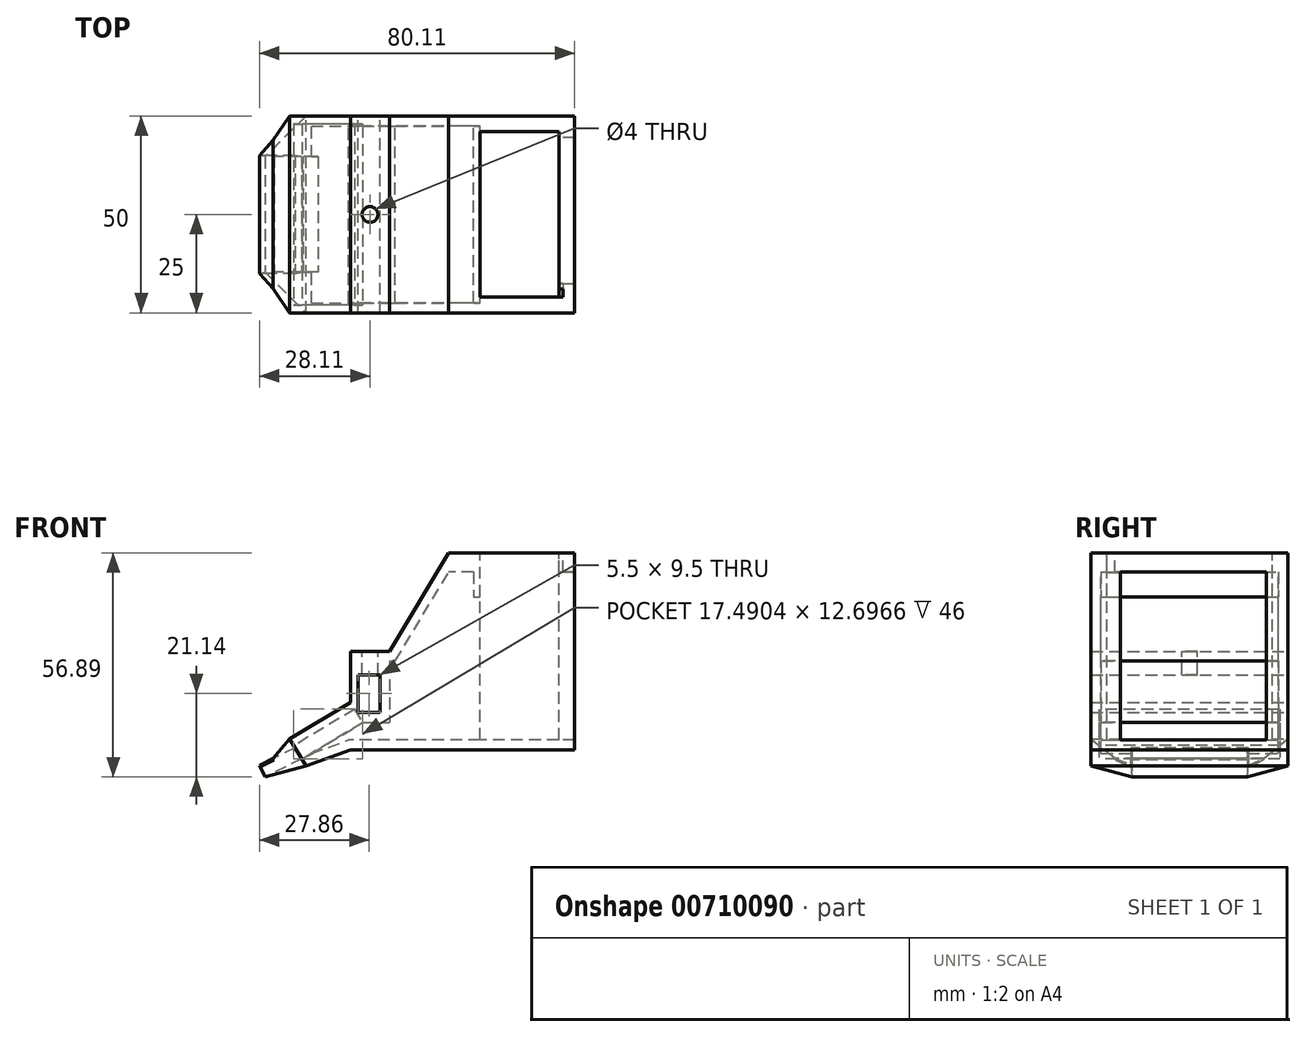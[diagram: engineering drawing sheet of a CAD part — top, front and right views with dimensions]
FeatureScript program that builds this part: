
annotation { "Feature Type Name" : "Feature", "Feature Type Description" : "" }
export const myFeature = defineFeature(function(context is Context, id is Id, definition is map)
    precondition{}
    {
        {
            var Q0;
            Q0=qCreatedBy(makeId("Front.planeOp"),FACE);
            var sketch = newSketch(context, id + "F0", { "sketchPlane" : qUnion([Q0])});
            skLineSegment(sketch, "E0", {"start": v(0, 0) * mm, "end": v(0, 25) * mm});
            skLineSegment(sketch, "E1", {"start": v(0, 25) * mm, "end": v(20, 25) * mm});
            skLineSegment(sketch, "E2", {"start": v(20, 25) * mm, "end": v(20, 0) * mm});
            skLineSegment(sketch, "E3", {"start": v(20, 0) * mm, "end": v(0, 0) * mm});
            skLineSegment(sketch, "E4.bottom", {"start": v(2, 19) * mm, "end": v(7.5, 19) * mm});
            skLineSegment(sketch, "E4.top", {"start": v(2, 9.5) * mm, "end": v(7.5, 9.5) * mm});
            skLineSegment(sketch, "E4.left", {"start": v(2, 19) * mm, "end": v(2, 9.5) * mm});
            skLineSegment(sketch, "E4.right", {"start": v(7.5, 19) * mm, "end": v(7.5, 9.5) * mm});
            skLineSegment(sketch, "E5", {"start": v(10, 25) * mm, "end": v(25, 50) * mm});
            skLineSegment(sketch, "E6", {"start": v(25, 50) * mm, "end": v(25, 0) * mm});
            skLineSegment(sketch, "E7", {"start": v(25, 0) * mm, "end": v(20, 0) * mm});
            skLineSegment(sketch, "E8", {"start": v(0, 12) * mm, "end": v(-15.4, 2.75) * mm});
            skLineSegment(sketch, "E9", {"start": v(-15.4, 2.75) * mm, "end": v(-11.28, -4.1) * mm});
            skLineSegment(sketch, "E10", {"start": v(-11.28, -4.1) * mm, "end": v(0, 0) * mm});
            skSolve(sketch);
        }
        {
            var Q0;
            Q0=makeQuery(id+"F0.imprint","IMPRINT",FACE,{"disambiguationData":[TD([[makeQuery(id+"F0.imprint","IMPRINT",EDGE,{"derivedFrom":sQuery(id+"F0.wireOp",EDGE,"E0")}),-1.0]])]});
            var Q1;
            {var subQ1=sQuery(id+"F0.wireOp",EDGE,"E2");Q1=makeQuery(id+"F0.imprint","IMPRINT",FACE,{"disambiguationData":[TD([[makeQuery(id+"F0.imprint","IMPRINT",EDGE,{"derivedFrom":subQ1}),1.0]])]});}
            var Q2;
            {var subQ2=sQuery(id+"F0.wireOp",EDGE,"E8");Q2=makeQuery(id+"F0.imprint","IMPRINT",FACE,{"disambiguationData":[TD([[makeQuery(id+"F0.imprint","IMPRINT",EDGE,{"derivedFrom":subQ2}),1.0]])]});}
            extrude(context, id + "F1", {"entities" : qUnion([Q0, Q1, Q2]), "depth" : 50 * mm, "offsetDistance" : 25 * mm});
        }
        {
            var Q0;
            Q0=makeQuery(id+"F1.opExtrude","SWEPT_FACE",FACE,{"disambiguationData":[OSD([sQuery(id+"F0.wireOp",EDGE,"E6")])]});
            shell(context, id + "F2", {"entities" : qUnion([Q0]), "thickness" : 2.5 * mm});
        }
        {
            var Q0;
            Q0=makeQuery(id+"F1.opExtrude","SWEPT_FACE",FACE,{"disambiguationData":[OSD([sQuery(id+"F0.wireOp",EDGE,"E9")])]});
            var sketch = newSketch(context, id + "F3", { "sketchPlane" : qUnion([Q0])});
            skLineSegment(sketch, "E11.bottom", {"start": v(2, 8.29) * mm, "end": v(48, 8.29) * mm});
            skLineSegment(sketch, "E11.top", {"start": v(2, 4.29) * mm, "end": v(48, 4.29) * mm});
            skLineSegment(sketch, "E11.left", {"start": v(2, 8.29) * mm, "end": v(2, 4.29) * mm});
            skLineSegment(sketch, "E11.right", {"start": v(48, 8.29) * mm, "end": v(48, 4.29) * mm});
            skSolve(sketch);
        }
        {
            var Q0;
            Q0=makeQuery(id+"F3.imprint","IMPRINT",FACE,{"disambiguationData":[TD([[makeQuery(id+"F3.imprint","IMPRINT",EDGE,{"derivedFrom":sQuery(id+"F3.wireOp",EDGE,"E11.bottom")}),-1.0]])]});
            extrude(context, id + "F4", {"entities" : qUnion([Q0]), "operationType" : NewBodyOperationType.REMOVE, "oppositeDirection" : true, "depth" : 18 * mm, "offsetDistance" : 25 * mm});
        }
        {
            var Q0;
            Q0=makeQuery(id+"F1.opExtrude","SWEPT_FACE",FACE,{"disambiguationData":[OSD([sQuery(id+"F0.wireOp",EDGE,"E6")])]});
            extrude(context, id + "F5", {"entities" : qUnion([Q0]), "operationType" : NewBodyOperationType.ADD, "depth" : 30 * mm, "offsetDistance" : 25 * mm});
        }
        {
            var Q0;
            {var subQ0=sQuery(id+"F0.wireOp",EDGE,"E6");var subQ1=sQuery(id+"F0.wireOp",EDGE,"E5");Q0=makeQuery(id+"F5.opExtrude","SWEPT_FACE",FACE,{"disambiguationData":[OSD([subQ1,subQ0]),TDD([makeQuery(id+"F2.opShell","OFFSET_EDGE",EDGE,{"disambiguationData":[OSD([subQ1,subQ0])]})])]});}
            var sketch = newSketch(context, id + "F6", { "sketchPlane" : qUnion([Q0])});
            skLineSegment(sketch, "E12", {"start": v(53, 47.5) * mm, "end": v(53, 2.5) * mm});
            skLineSegment(sketch, "E13", {"start": v(53, 44.5) * mm, "end": v(55, 44.5) * mm});
            skLineSegment(sketch, "E14", {"start": v(55, 44.5) * mm, "end": v(55, 5.5) * mm});
            skLineSegment(sketch, "E15", {"start": v(55, 5.5) * mm, "end": v(53, 5.5) * mm});
            skSolve(sketch);
        }
        {
            var Q0;
            {var subQ5=sQuery(id+"F6.wireOp",EDGE,"E13");Q0=makeQuery(id+"F6.imprint","IMPRINT",FACE,{"disambiguationData":[TD([[makeQuery(id+"F6.imprint","IMPRINT",EDGE,{"derivedFrom":subQ5}),1.0]])]});}
            var Q1;
            {var subQ5=sQuery(id+"F6.wireOp",EDGE,"E15");Q1=makeQuery(id+"F6.imprint","IMPRINT",FACE,{"disambiguationData":[TD([[makeQuery(id+"F6.imprint","IMPRINT",EDGE,{"derivedFrom":subQ5}),1.0]])]});}
            extrude(context, id + "F7", {"entities" : qUnion([Q0, Q1]), "operationType" : NewBodyOperationType.ADD, "endBound" : BoundingType.UP_TO_NEXT, "depth" : 25 * mm, "offsetDistance" : 25 * mm});
        }
        {
            var Q0;
            {var subQ0=sQuery(id+"F0.wireOp",EDGE,"E6");var subQ1=sQuery(id+"F0.wireOp",EDGE,"E5");Q0=makeQuery(id+"F5.opExtrude","SWEPT_FACE",FACE,{"disambiguationData":[OSD([subQ1,subQ0]),TDD([makeQuery(id+"F1.opExtrude","SWEPT_EDGE",EDGE,{"disambiguationData":[OSD([subQ1,subQ0])]})])]});}
            var sketch = newSketch(context, id + "F8", { "sketchPlane" : qUnion([Q0])});
            skLineSegment(sketch, "E16.bottom", {"start": v(33, -46) * mm, "end": v(53, -46) * mm});
            skLineSegment(sketch, "E16.top", {"start": v(33, -4) * mm, "end": v(53, -4) * mm});
            skLineSegment(sketch, "E16.left", {"start": v(33, -46) * mm, "end": v(33, -4) * mm});
            skLineSegment(sketch, "E16.right", {"start": v(53, -46) * mm, "end": v(53, -4) * mm});
            skSolve(sketch);
        }
        {
            var Q0;
            Q0=makeQuery(id+"F8.imprint","IMPRINT",FACE,{"disambiguationData":[TD([[makeQuery(id+"F8.imprint","IMPRINT",EDGE,{"derivedFrom":sQuery(id+"F8.wireOp",EDGE,"E16.bottom")}),1.0]])]});
            extrude(context, id + "F9", {"entities" : qUnion([Q0]), "operationType" : NewBodyOperationType.REMOVE, "endBound" : BoundingType.UP_TO_NEXT, "oppositeDirection" : true, "depth" : 25 * mm, "offsetDistance" : 25 * mm});
        }
        {
            var Q0;
            {var subQ0=sQuery(id+"F0.wireOp",EDGE,"E6");var subQ1=sQuery(id+"F0.wireOp",EDGE,"E10");var subQ2=sQuery(id+"F0.wireOp",EDGE,"E9");var subQ3=sQuery(id+"F0.wireOp",EDGE,"E8");var subQ4=sQuery(id+"F0.wireOp",EDGE,"E7");var subQ5=sQuery(id+"F0.wireOp",EDGE,"E5");var subQ6=sQuery(id+"F0.wireOp",EDGE,"E4.right");var subQ7=sQuery(id+"F0.wireOp",EDGE,"E4.left");var subQ8=sQuery(id+"F0.wireOp",EDGE,"E4.top");var subQ9=sQuery(id+"F0.wireOp",EDGE,"E4.bottom");var subQ10=sQuery(id+"F0.wireOp",EDGE,"E3");var subQ11=sQuery(id+"F0.wireOp",EDGE,"E1");var subQ12=sQuery(id+"F0.wireOp",EDGE,"E0");Q0=makeQuery(id+"F5.boolean.opBoolean","MERGE",FACE,{"derivedFrom":[makeQuery(id+"F2.opShell","OFFSET_FACE",FACE,{"disambiguationData":[OSD([subQ12,subQ11,subQ10,subQ9,subQ8,subQ7,subQ6,subQ5,subQ0,subQ4,subQ3,subQ2,subQ1]),TDD([makeQuery(id+"F1.opExtrude","CAP_FACE",FACE,{"disambiguationData":[OSD([subQ12,subQ11,subQ10,subQ9,subQ8,subQ7,subQ6,subQ5,subQ0,subQ4,subQ3,subQ2,subQ1])],"isStart":true})])]}),makeQuery(id+"F5.opExtrude","SWEPT_FACE",FACE,{"disambiguationData":[OSD([subQ0]),TDD([makeQuery(id+"F2.opShell","OFFSET_EDGE",EDGE,{"disambiguationData":[OSD([subQ0]),TDD([makeQuery(id+"F1.opExtrude","CAP_EDGE",EDGE,{"disambiguationData":[OSD([subQ0])],"isStart":true})])]})])]})]});}
            var sketch = newSketch(context, id + "F10", { "sketchPlane" : qUnion([Q0])});
            skLineSegment(sketch, "E17.bottom", {"start": v(31.3, 45.14) * mm, "end": v(33, 45.14) * mm});
            skLineSegment(sketch, "E17.top", {"start": v(31.3, 41.86) * mm, "end": v(33, 41.86) * mm});
            skLineSegment(sketch, "E17.left", {"start": v(31.3, 45.14) * mm, "end": v(31.3, 41.86) * mm});
            skLineSegment(sketch, "E17.right", {"start": v(33, 45.14) * mm, "end": v(33, 41.86) * mm});
            skSolve(sketch);
        }
        {
            var Q0;
            Q0=makeQuery(id+"F10.imprint","IMPRINT",FACE,{"disambiguationData":[TD([[makeQuery(id+"F10.imprint","IMPRINT",EDGE,{"derivedFrom":sQuery(id+"F10.wireOp",EDGE,"E17.bottom")}),1.0]])]});
            extrude(context, id + "F11", {"entities" : qUnion([Q0]), "operationType" : NewBodyOperationType.ADD, "endBound" : BoundingType.UP_TO_NEXT, "depth" : 25 * mm, "offsetDistance" : 25 * mm});
        }
        {
            var Q0;
            {var subQ0=sQuery(id+"F0.wireOp",EDGE,"E6");var subQ1=sQuery(id+"F0.wireOp",EDGE,"E5");Q0=makeQuery(id+"F5.opExtrude","SWEPT_FACE",FACE,{"disambiguationData":[OSD([subQ1,subQ0]),TDD([makeQuery(id+"F1.opExtrude","SWEPT_EDGE",EDGE,{"disambiguationData":[OSD([subQ1,subQ0])]})])]});}
            var sketch = newSketch(context, id + "F12", { "sketchPlane" : qUnion([Q0])});
            skLineSegment(sketch, "E18.bottom", {"start": v(53, -46) * mm, "end": v(54, -46) * mm});
            skLineSegment(sketch, "E18.top", {"start": v(53, -44) * mm, "end": v(54, -44) * mm});
            skLineSegment(sketch, "E18.left", {"start": v(53, -46) * mm, "end": v(53, -44) * mm});
            skLineSegment(sketch, "E18.right", {"start": v(54, -46) * mm, "end": v(54, -44) * mm});
            skSolve(sketch);
        }
        {
            var Q0;
            Q0=makeQuery(id+"F12.imprint","IMPRINT",FACE,{"disambiguationData":[TD([[makeQuery(id+"F12.imprint","IMPRINT",EDGE,{"derivedFrom":sQuery(id+"F12.wireOp",EDGE,"E18.bottom")}),1.0]])]});
            extrude(context, id + "F13", {"entities" : qUnion([Q0]), "operationType" : NewBodyOperationType.REMOVE, "oppositeDirection" : true, "depth" : 5 * mm, "offsetDistance" : 25 * mm});
        }
        {
            var Q0;
            {var subQ1=sQuery(id+"F0.wireOp",EDGE,"E6");var subQ2=sQuery(id+"F0.wireOp",EDGE,"E5");var subQ19=makeQuery(id+"F9.opExtrude","SWEPT_FACE",FACE,{"disambiguationData":[OSD([sQuery(id+"F8.wireOp",EDGE,"E16.bottom")])]});Q0=makeQuery(id+"F11.boolean.opBoolean","SPLIT",FACE,{"disambiguationData":[TD([makeQuery(id+"F9.boolean.opBoolean","COPY",FACE,{"derivedFrom":subQ19})])],"derivedFrom":makeQuery(id+"F9.boolean.opBoolean","SPLIT",FACE,{"disambiguationData":[TD([makeQuery(id+"F2.opShell","OFFSET_FACE",FACE,{"disambiguationData":[OSD([subQ2])]})])],"derivedFrom":makeQuery(id+"F5.opExtrude","SWEPT_FACE",FACE,{"disambiguationData":[OSD([subQ2,subQ1]),TDD([makeQuery(id+"F2.opShell","OFFSET_EDGE",EDGE,{"disambiguationData":[OSD([subQ2,subQ1])]})])]})})});}
            var Q1;
            {var subQ1=sQuery(id+"F0.wireOp",EDGE,"E6");var subQ2=sQuery(id+"F0.wireOp",EDGE,"E5");var subQ4=makeQuery(id+"F9.opExtrude","SWEPT_FACE",FACE,{"disambiguationData":[OSD([sQuery(id+"F8.wireOp",EDGE,"E16.top")])]});Q1=makeQuery(id+"F11.boolean.opBoolean","SPLIT",FACE,{"disambiguationData":[TD([makeQuery(id+"F9.boolean.opBoolean","COPY",FACE,{"derivedFrom":subQ4})])],"derivedFrom":makeQuery(id+"F9.boolean.opBoolean","SPLIT",FACE,{"disambiguationData":[TD([makeQuery(id+"F2.opShell","OFFSET_FACE",FACE,{"disambiguationData":[OSD([subQ2])]})])],"derivedFrom":makeQuery(id+"F5.opExtrude","SWEPT_FACE",FACE,{"disambiguationData":[OSD([subQ2,subQ1]),TDD([makeQuery(id+"F2.opShell","OFFSET_EDGE",EDGE,{"disambiguationData":[OSD([subQ2,subQ1])]})])]})})});}
            extrude(context, id + "F14", {"entities" : qUnion([Q0, Q1]), "operationType" : NewBodyOperationType.ADD, "endBound" : BoundingType.UP_TO_NEXT, "depth" : 25 * mm, "offsetDistance" : 25 * mm});
        }
        {
            var Q0;
            {var subQ0=sQuery(id+"F0.wireOp",EDGE,"E6");var subQ1=sQuery(id+"F0.wireOp",EDGE,"E5");var subQ2=makeQuery(id+"F5.opExtrude","CAP_EDGE",EDGE,{"disambiguationData":[OSD([subQ1,subQ0]),TDD([makeQuery(id+"F2.opShell","OFFSET_EDGE",EDGE,{"disambiguationData":[OSD([subQ1,subQ0])]})])],"isStart":false});var subQ3=sQuery(id+"F6.wireOp",EDGE,"E14");Q0=makeQuery(id+"F7.boolean.opBoolean","MERGE",FACE,{"derivedFrom":[makeQuery(id+"F5.opExtrude","CAP_FACE",FACE,{"disambiguationData":[OSD([subQ0])],"isStart":false}),makeQuery(id+"F7.opExtrude","SWEPT_FACE",FACE,{"disambiguationData":[OSD([subQ1,subQ0]),TDD([makeQuery(id+"F6.imprint","IMPRINT",EDGE,{"disambiguationData":[TD([[makeQuery(id+"F6.imprint","INTERSECT",VERTEX,{"derivedFrom":[subQ2,subQ3,sQuery(id+"F6.wireOp",EDGE,"E15")]}),-1.0]])],"derivedFrom":subQ2})])]}),makeQuery(id+"F7.opExtrude","SWEPT_FACE",FACE,{"disambiguationData":[OSD([subQ1,subQ0]),TDD([makeQuery(id+"F6.imprint","IMPRINT",EDGE,{"disambiguationData":[TD([[makeQuery(id+"F6.imprint","INTERSECT",VERTEX,{"derivedFrom":[subQ2,sQuery(id+"F6.wireOp",EDGE,"E13"),subQ3]}),1.0]])],"derivedFrom":subQ2})])]})]});}
            extrude(context, id + "F15", {"entities" : qUnion([Q0]), "operationType" : NewBodyOperationType.ADD, "depth" : 5 * mm, "offsetDistance" : 25 * mm});
        }
        {
            var Q0;
            Q0=makeQuery(id+"F11.opExtrude","SWEPT_FACE",FACE,{"disambiguationData":[OSD([sQuery(id+"F10.wireOp",EDGE,"E17.top")])]});
            extrude(context, id + "F16", {"entities" : qUnion([Q0]), "operationType" : NewBodyOperationType.ADD, "depth" : 3 * mm, "offsetDistance" : 25 * mm});
        }
        {
            var Q0;
            {var subQ0=sQuery(id+"F6.wireOp",EDGE,"E13");Q0=makeQuery(id+"F15.boolean.opBoolean","MERGE",FACE,{"derivedFrom":[makeQuery(id+"F7.opExtrude","SWEPT_FACE",FACE,{"disambiguationData":[OSD([subQ0])]}),makeQuery(id+"F15.opExtrude","SWEPT_FACE",FACE,{"disambiguationData":[OSD([sQuery(id+"F0.wireOp",EDGE,"E5"),sQuery(id+"F0.wireOp",EDGE,"E6"),subQ0,sQuery(id+"F6.wireOp",EDGE,"E14")])]})]});}
            extrude(context, id + "F17", {"entities" : qUnion([Q0]), "operationType" : NewBodyOperationType.ADD, "depth" : 2 * mm, "offsetDistance" : 25 * mm});
        }
        {
            var Q0;
            Q0=makeQuery(id+"F1.opExtrude","SWEPT_FACE",FACE,{"disambiguationData":[OSD([sQuery(id+"F0.wireOp",EDGE,"E8")])]});
            var sketch = newSketch(context, id + "F18", { "sketchPlane" : qUnion([Q0])});
            skLineSegment(sketch, "E19", {"start": v(-11.78, -50) * mm, "end": v(-33.78, -28) * mm});
            skLineSegment(sketch, "E20", {"start": v(-33.78, -28) * mm, "end": v(-33.78, -22) * mm});
            skLineSegment(sketch, "E21", {"start": v(-33.78, -22) * mm, "end": v(-11.78, 0) * mm});
            skLineSegment(sketch, "E22", {"start": v(-11.78, 0) * mm, "end": v(-33.78, 0) * mm});
            skLineSegment(sketch, "E23", {"start": v(-33.78, 0) * mm, "end": v(-33.78, -22) * mm});
            skLineSegment(sketch, "E24", {"start": v(-11.78, -50) * mm, "end": v(-33.78, -50) * mm});
            skLineSegment(sketch, "E25", {"start": v(-33.78, -50) * mm, "end": v(-33.78, -28) * mm});
            skSolve(sketch);
        }
        {
            var Q0;
            {var subQ0=sQuery(id+"F0.wireOp",EDGE,"E6");var subQ1=makeQuery(id+"F1.opExtrude","CAP_EDGE",EDGE,{"disambiguationData":[OSD([subQ0])],"isStart":false});Q0=makeQuery(id+"F15.boolean.opBoolean","MERGE",FACE,{"derivedFrom":[makeQuery(id+"F5.boolean.opBoolean","MERGE",FACE,{"derivedFrom":[makeQuery(id+"F1.opExtrude","CAP_FACE",FACE,{"disambiguationData":[OSD([sQuery(id+"F0.wireOp",EDGE,"E0"),sQuery(id+"F0.wireOp",EDGE,"E1"),sQuery(id+"F0.wireOp",EDGE,"E3"),sQuery(id+"F0.wireOp",EDGE,"E4.bottom"),sQuery(id+"F0.wireOp",EDGE,"E4.top"),sQuery(id+"F0.wireOp",EDGE,"E4.left"),sQuery(id+"F0.wireOp",EDGE,"E4.right"),sQuery(id+"F0.wireOp",EDGE,"E5"),subQ0,sQuery(id+"F0.wireOp",EDGE,"E7"),sQuery(id+"F0.wireOp",EDGE,"E8"),sQuery(id+"F0.wireOp",EDGE,"E9"),sQuery(id+"F0.wireOp",EDGE,"E10")])],"isStart":false}),makeQuery(id+"F5.opExtrude","SWEPT_FACE",FACE,{"disambiguationData":[OSD([subQ0]),TDD([subQ1])]})]}),makeQuery(id+"F15.opExtrude","SWEPT_FACE",FACE,{"disambiguationData":[OSD([subQ0]),TDD([makeQuery(id+"F5.opExtrude","CAP_EDGE",EDGE,{"disambiguationData":[OSD([subQ0]),TDD([subQ1])],"isStart":false})])]})]});}
            var sketch = newSketch(context, id + "F19", { "sketchPlane" : qUnion([Q0])});
            skLineSegment(sketch, "E26", {"start": v(-15.4, 2.75) * mm, "end": v(-19.6, -2.2) * mm});
            skLineSegment(sketch, "E27", {"start": v(-19.6, -2.2) * mm, "end": v(-23.1, -3.92) * mm});
            skLineSegment(sketch, "E28", {"start": v(-23.1, -3.92) * mm, "end": v(-21.67, -6.89) * mm});
            skLineSegment(sketch, "E29", {"start": v(-21.67, -6.89) * mm, "end": v(-11.28, -4.1) * mm});
            skSolve(sketch);
        }
        {
            var Q0;
            Q0=makeQuery(id+"F19.imprint","IMPRINT",FACE,{"disambiguationData":[TD([[makeQuery(id+"F19.imprint","IMPRINT",EDGE,{"derivedFrom":sQuery(id+"F19.wireOp",EDGE,"E26")}),1.0]])]});
            extrude(context, id + "F20", {"entities" : qUnion([Q0]), "operationType" : NewBodyOperationType.ADD, "oppositeDirection" : true, "depth" : 50 * mm, "offsetDistance" : 25 * mm});
        }
        {
            var Q0;
            Q0=makeQuery(id+"F18.imprint","IMPRINT",FACE,{"disambiguationData":[TD([[makeQuery(id+"F18.imprint","IMPRINT",EDGE,{"derivedFrom":sQuery(id+"F18.wireOp",EDGE,"E19")}),1.0]])]});
            var Q1;
            Q1=makeQuery(id+"F18.imprint","IMPRINT",FACE,{"disambiguationData":[TD([[makeQuery(id+"F18.imprint","IMPRINT",EDGE,{"derivedFrom":sQuery(id+"F18.wireOp",EDGE,"E21")}),1.0]])]});
            extrude(context, id + "F21", {"entities" : qUnion([Q0, Q1]), "operationType" : NewBodyOperationType.REMOVE, "oppositeDirection" : true, "depth" : 25 * mm, "offsetDistance" : 25 * mm});
        }
        {
            var Q0;
            Q0=makeQuery(id+"F20.opExtrude","SWEPT_FACE",FACE,{"disambiguationData":[OSD([sQuery(id+"F19.wireOp",EDGE,"E28")])]});
            extrude(context, id + "F22", {"entities" : qUnion([Q0]), "operationType" : NewBodyOperationType.REMOVE, "oppositeDirection" : true, "depth" : 15 * mm, "offsetDistance" : 25 * mm});
        }
        {
            var Q0;
            Q0=makeQuery(id+"F20.opExtrude","SWEPT_FACE",FACE,{"disambiguationData":[OSD([sQuery(id+"F19.wireOp",EDGE,"E27")])]});
            extrude(context, id + "F23", {"entities" : qUnion([Q0]), "operationType" : NewBodyOperationType.ADD, "oppositeDirection" : true, "depth" : 0.5 * mm, "offsetDistance" : 25 * mm});
        }
        {
            var Q0;
            {var subQ0=sQuery(id+"F6.wireOp",EDGE,"E14");var subQ1=sQuery(id+"F6.wireOp",EDGE,"E13");var subQ2=sQuery(id+"F0.wireOp",EDGE,"E6");var subQ3=sQuery(id+"F0.wireOp",EDGE,"E5");Q0=makeQuery(id+"F17.boolean.opBoolean","MERGE",FACE,{"derivedFrom":[makeQuery(id+"F15.opExtrude","CAP_FACE",FACE,{"disambiguationData":[OSD([subQ3,subQ2])],"isStart":false}),makeQuery(id+"F17.opExtrude","SWEPT_FACE",FACE,{"disambiguationData":[OSD([subQ3,subQ2,subQ1,subQ0]),TDD([makeQuery(id+"F15.opExtrude","CAP_EDGE",EDGE,{"disambiguationData":[OSD([subQ3,subQ2,subQ1,subQ0])],"isStart":false})])]})]});}
            extrude(context, id + "F24", {"entities" : qUnion([Q0]), "operationType" : NewBodyOperationType.REMOVE, "oppositeDirection" : true, "depth" : 3 * mm, "offsetDistance" : 25 * mm});
        }
        {
            var Q0;
            Q0=makeQuery(id+"F2.opShell","OFFSET_FACE",FACE,{"disambiguationData":[OSD([sQuery(id+"F0.wireOp",EDGE,"E4.bottom")])]});
            extrude(context, id + "F25", {"entities" : qUnion([Q0]), "operationType" : NewBodyOperationType.ADD, "depth" : 2 * mm, "offsetDistance" : 25 * mm});
        }
        {
            var Q0;
            Q0=makeQuery(id+"F1.opExtrude","SWEPT_FACE",FACE,{"disambiguationData":[OSD([sQuery(id+"F0.wireOp",EDGE,"E1")])]});
            var sketch = newSketch(context, id + "F26", { "sketchPlane" : qUnion([Q0])});
            skCircle(sketch, "E30", {"center": v(5, -25) * mm, "radius": 2 * mm});
            skSolve(sketch);
        }
        {
            var Q0;
            Q0=makeQuery(id+"F26.imprint","IMPRINT",FACE,{"disambiguationData":[TD([[makeQuery(id+"F26.imprint","IMPRINT",EDGE,{"derivedFrom":sQuery(id+"F26.wireOp",EDGE,"E30")}),1.0]])]});
            extrude(context, id + "F27", {"entities" : qUnion([Q0]), "operationType" : NewBodyOperationType.REMOVE, "oppositeDirection" : true, "depth" : 6 * mm, "offsetDistance" : 25 * mm});
        }
    });
